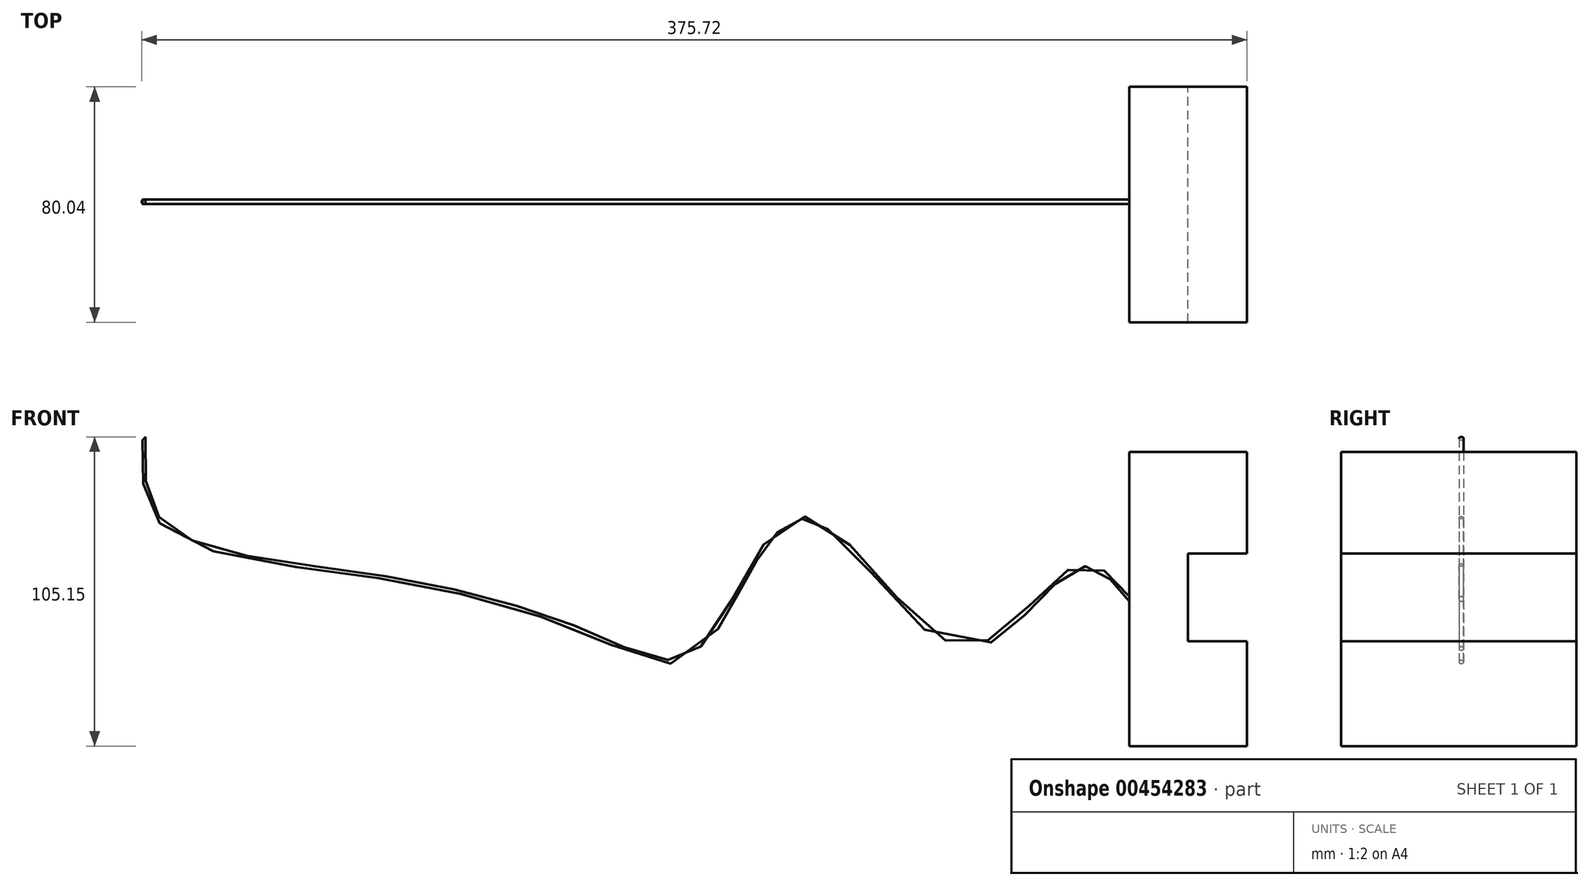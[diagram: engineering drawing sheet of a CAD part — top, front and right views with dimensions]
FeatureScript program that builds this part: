
annotation { "Feature Type Name" : "Feature", "Feature Type Description" : "" }
export const myFeature = defineFeature(function(context is Context, id is Id, definition is map)
    precondition{}
    {
        {
            var Q0;
            Q0=qCreatedBy(makeId("Right.planeOp"),FACE);
            var sketch = newSketch(context, id + "F0", { "sketchPlane" : qUnion([Q0])});
            skLineSegment(sketch, "E0", {"start": v(0, 0) * mm, "end": v(-40.02, 0) * mm});
            skLineSegment(sketch, "E1", {"start": v(-40.02, 0) * mm, "end": v(-40.02, 50.04) * mm});
            skLineSegment(sketch, "E2", {"start": v(-40.02, 50.04) * mm, "end": v(0, 50.04) * mm});
            skLineSegment(sketch, "E3.MirrorCS", {"start": v(40.02, 50.04) * mm, "end": v(0, 50.04) * mm});
            skLineSegment(sketch, "E4.MirrorCS", {"start": v(40.02, 0) * mm, "end": v(40.02, 50.04) * mm});
            skLineSegment(sketch, "E5.MirrorCS", {"start": v(0, 0) * mm, "end": v(40.02, 0) * mm});
            skLineSegment(sketch, "E6.MirrorCS", {"start": v(-40.02, -50.04) * mm, "end": v(0, -50.04) * mm});
            skLineSegment(sketch, "E7.MirrorCS", {"start": v(-40.02, 0) * mm, "end": v(-40.02, -50.04) * mm});
            skLineSegment(sketch, "E8.MirrorCS", {"start": v(40.02, 0) * mm, "end": v(40.02, -50.04) * mm});
            skLineSegment(sketch, "E9.MirrorCS", {"start": v(40.02, -50.04) * mm, "end": v(0, -50.04) * mm});
            skSolve(sketch);
        }
        {
            var Q0;
            Q0=makeQuery(id+"F0.imprint","IMPRINT",FACE,{"disambiguationData":[TD([[makeQuery(id+"F0.imprint","IMPRINT",EDGE,{"derivedFrom":sQuery(id+"F0.wireOp",EDGE,"E0")}),1.0]])]});
            var Q1;
            Q1=makeQuery(id+"F0.imprint","IMPRINT",FACE,{"disambiguationData":[TD([[makeQuery(id+"F0.imprint","IMPRINT",EDGE,{"derivedFrom":sQuery(id+"F0.wireOp",EDGE,"E0")}),-1.0]])]});
            extrude(context, id + "F1", {"entities" : qUnion([Q0, Q1]), "oppositeDirection" : true, "depth" : 40 * mm, "offsetDistance" : 25 * mm});
        }
        {
            var Q0;
            Q0=makeQuery(id+"F1.opExtrude","CAP_FACE",FACE,{"disambiguationData":[OSD([sQuery(id+"F0.wireOp",EDGE,"E1"),sQuery(id+"F0.wireOp",EDGE,"E2"),sQuery(id+"F0.wireOp",EDGE,"E3.MirrorCS"),sQuery(id+"F0.wireOp",EDGE,"E4.MirrorCS"),sQuery(id+"F0.wireOp",EDGE,"E6.MirrorCS"),sQuery(id+"F0.wireOp",EDGE,"E7.MirrorCS"),sQuery(id+"F0.wireOp",EDGE,"E8.MirrorCS"),sQuery(id+"F0.wireOp",EDGE,"E9.MirrorCS")])],"isStart":true});
            var sketch = newSketch(context, id + "F2", { "sketchPlane" : qUnion([Q0])});
            skLineSegment(sketch, "E10", {"start": v(-40.02, 0) * mm, "end": v(-40.02, 15.4) * mm});
            skLineSegment(sketch, "E11", {"start": v(-40.02, 15.4) * mm, "end": v(40.02, 15.4) * mm});
            skLineSegment(sketch, "E12", {"start": v(40.02, 15.4) * mm, "end": v(40.02, -14.38) * mm});
            skLineSegment(sketch, "E13", {"start": v(40.02, -14.38) * mm, "end": v(-40.02, -14.38) * mm});
            skLineSegment(sketch, "E14", {"start": v(-40.02, -14.38) * mm, "end": v(-40.02, 0) * mm});
            skSolve(sketch);
        }
        {
            var Q0;
            Q0=makeQuery(id+"F2.imprint","IMPRINT",FACE,{"disambiguationData":[TD([[makeQuery(id+"F2.imprint","IMPRINT",EDGE,{"derivedFrom":sQuery(id+"F2.wireOp",EDGE,"E10")}),1.0]])]});
            extrude(context, id + "F3", {"entities" : qUnion([Q0]), "operationType" : NewBodyOperationType.REMOVE, "oppositeDirection" : true, "depth" : 20 * mm, "offsetDistance" : 25 * mm});
        }
        {
            var Q0;
            Q0=makeQuery(id+"F1.opExtrude","CAP_FACE",FACE,{"disambiguationData":[OSD([sQuery(id+"F0.wireOp",EDGE,"E1"),sQuery(id+"F0.wireOp",EDGE,"E2"),sQuery(id+"F0.wireOp",EDGE,"E3.MirrorCS"),sQuery(id+"F0.wireOp",EDGE,"E4.MirrorCS"),sQuery(id+"F0.wireOp",EDGE,"E6.MirrorCS"),sQuery(id+"F0.wireOp",EDGE,"E7.MirrorCS"),sQuery(id+"F0.wireOp",EDGE,"E8.MirrorCS"),sQuery(id+"F0.wireOp",EDGE,"E9.MirrorCS")])],"isStart":false});
            var sketch = newSketch(context, id + "F4", { "sketchPlane" : qUnion([Q0])});
            skCircle(sketch, "E15", {"center": v(-0.94, 0) * mm, "radius": 0.8 * mm});
            skSolve(sketch);
        }
        {
            var Q0;
            Q0=qCreatedBy(makeId("Front.planeOp"),FACE);
            var sketch = newSketch(context, id + "F5", { "sketchPlane" : qUnion([Q0])});
            skFitSpline(sketch, "E16", {"points": [v(-42.55, 0.8) * mm, v(-57.67, 9.2) * mm, v(-97.18, -17.96) * mm, v(-150.96, 25.9) * mm, v(-185.96, -18.99) * mm, v(-222.65, -13.68) * mm, v(-297.53, 6.43) * mm, v(-369.35, 24.39) * mm, v(-376.3, 56.84) * mm], "startDerivative": vector(-184.48, 217.8) * mm, "endDerivative": vector(17.23, 359.65) * mm});
            skSolve(sketch);
        }
        {
            var Q0;
            Q0=makeQuery(id+"F4.imprint","IMPRINT",FACE,{"disambiguationData":[TD([[makeQuery(id+"F4.imprint","IMPRINT",EDGE,{"derivedFrom":sQuery(id+"F4.wireOp",EDGE,"E15")}),1.0]])]});
            var Q1;
            Q1=sQuery(id+"F5.wireOp",EDGE,"E16");
            sweep(context, id + "F6", {"operationType" : NewBodyOperationType.ADD, "profiles" : qUnion([Q0]), "path" : qUnion([Q1])});
        }
    });
